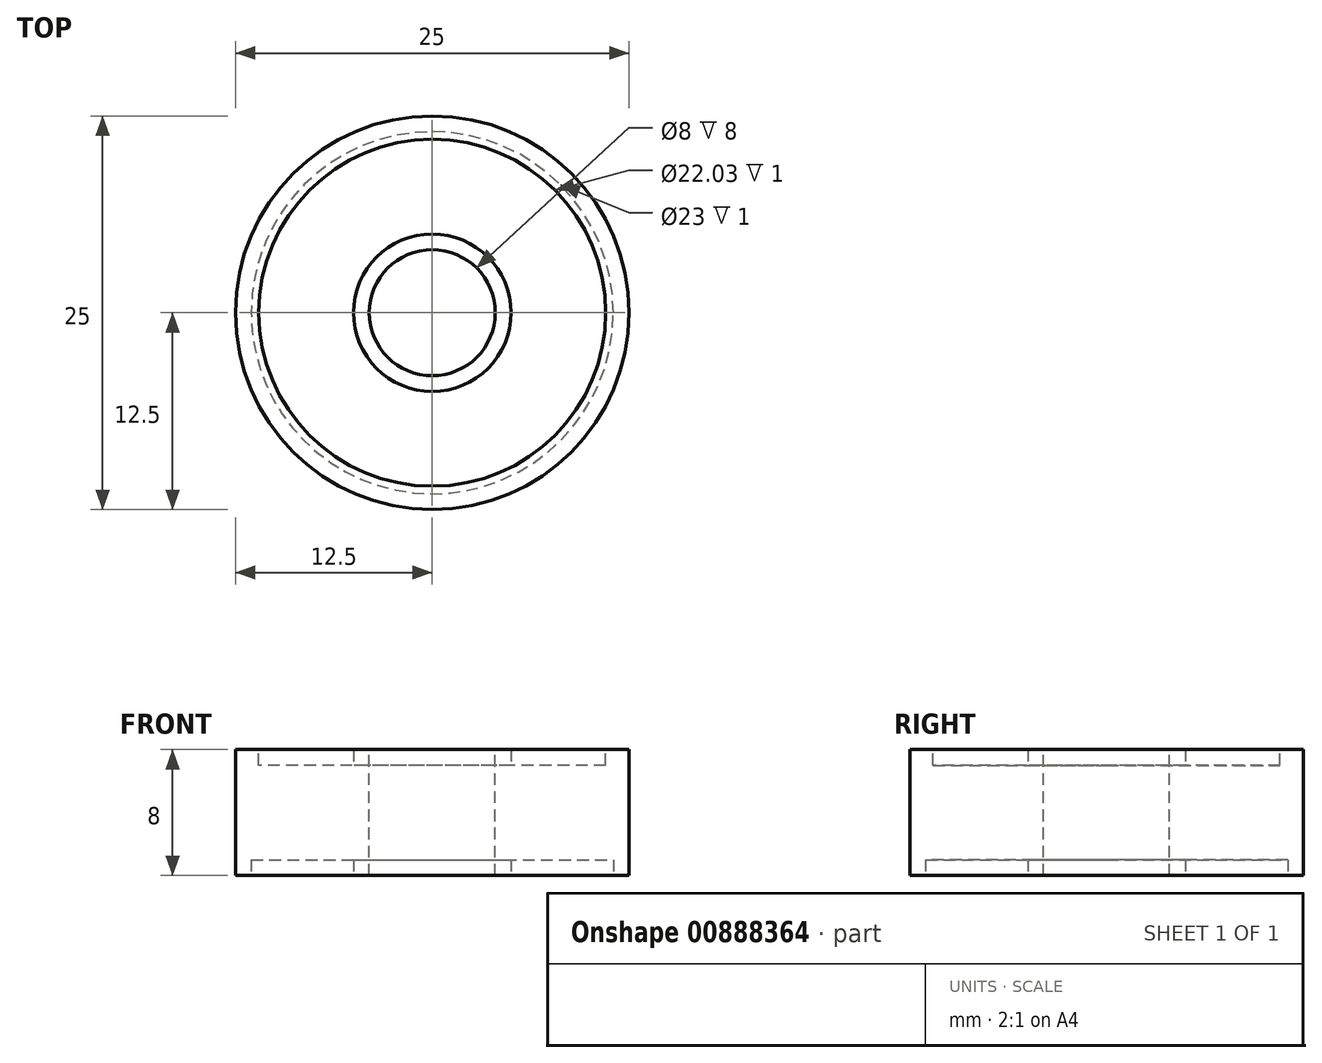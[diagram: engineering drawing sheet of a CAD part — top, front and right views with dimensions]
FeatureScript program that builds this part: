
annotation { "Feature Type Name" : "Feature", "Feature Type Description" : "" }
export const myFeature = defineFeature(function(context is Context, id is Id, definition is map)
    precondition{}
    {
        {
            var Q0;
            Q0=qCreatedBy(makeId("Top.planeOp"),FACE);
            var sketch = newSketch(context, id + "F0", { "sketchPlane" : qUnion([Q0])});
            skCircle(sketch, "E0", {"center": v(0, 0) * mm, "radius": 12.5 * mm});
            skCircle(sketch, "E1", {"center": v(0, 0) * mm, "radius": 11.5 * mm});
            skSolve(sketch);
        }
        {
            var Q0;
            Q0 = qSketchRegion(id + "F0", true);
            var Q1;
            Q1=makeQuery(id+"F0.imprint","IMPRINT",FACE,{"disambiguationData":[TD([[makeQuery(id+"F0.imprint","IMPRINT",EDGE,{"derivedFrom":sQuery(id+"F0.wireOp",EDGE,"E1")}),1.0]])]});
            extrude(context, id + "F1", {"entities" : qUnion([Q0, Q1]), "depth" : 8 * mm, "offsetDistance" : 25.4 * mm});
        }
        {
            var Q0;
            Q0=makeQuery(id+"F1.opExtrude","CAP_FACE",FACE,{"disambiguationData":[OSD([sQuery(id+"F0.wireOp",EDGE,"E0")])],"isStart":false});
            var sketch = newSketch(context, id + "F2", { "sketchPlane" : qUnion([Q0])});
            skCircle(sketch, "E2", {"center": v(0, 0) * mm, "radius": 11.02 * mm});
            skSolve(sketch);
        }
        {
            var Q0;
            Q0=makeQuery(id+"F2.imprint","IMPRINT",FACE,{"disambiguationData":[TD([[makeQuery(id+"F2.imprint","IMPRINT",EDGE,{"derivedFrom":sQuery(id+"F2.wireOp",EDGE,"E2")}),1.0]])]});
            var sketch = newSketch(context, id + "F3", { "sketchPlane" : qUnion([Q0])});
            skCircle(sketch, "E3", {"center": v(0, 0) * mm, "radius": 4 * mm});
            skCircle(sketch, "E4", {"center": v(0, 0) * mm, "radius": 5 * mm});
            skSolve(sketch);
        }
        {
            var Q0;
            Q0=makeQuery(id+"F3.imprint","IMPRINT",FACE,{"disambiguationData":[TD([[makeQuery(id+"F3.imprint","IMPRINT",EDGE,{"derivedFrom":sQuery(id+"F3.wireOp",EDGE,"E3")}),1.0]])]});
            extrude(context, id + "F4", {"entities" : qUnion([Q0]), "operationType" : NewBodyOperationType.REMOVE, "endBound" : BoundingType.THROUGH_ALL, "oppositeDirection" : true, "depth" : 25.4 * mm, "offsetDistance" : 25.4 * mm});
        }
        {
            var Q0;
            Q0=makeQuery(id+"F2.imprint","IMPRINT",FACE,{"disambiguationData":[TD([[makeQuery(id+"F2.imprint","IMPRINT",EDGE,{"derivedFrom":sQuery(id+"F2.wireOp",EDGE,"E2")}),1.0]])]});
            extrude(context, id + "F5", {"entities" : qUnion([Q0]), "operationType" : NewBodyOperationType.REMOVE, "oppositeDirection" : true, "depth" : 1 * mm, "offsetDistance" : 25.4 * mm});
        }
        {
            var Q0;
            Q0=makeQuery(id+"F5.boolean.opBoolean","COPY",FACE,{"derivedFrom":makeQuery(id+"F5.opExtrude","CAP_FACE",FACE,{"disambiguationData":[OSD([sQuery(id+"F2.wireOp",EDGE,"E2")])],"isStart":false})});
            var sketch = newSketch(context, id + "F6", { "sketchPlane" : qUnion([Q0])});
            skCircle(sketch, "E5", {"center": v(0, 0) * mm, "radius": 5 * mm});
            skSolve(sketch);
        }
        {
            var Q0;
            Q0=makeQuery(id+"F6.imprint","IMPRINT",FACE,{"disambiguationData":[TD([[makeQuery(id+"F6.imprint","IMPRINT",EDGE,{"derivedFrom":sQuery(id+"F6.wireOp",EDGE,"E5")}),1.0]])]});
            var Q1;
            Q1=sQuery(id+"F6.wireOp",EDGE,"E5");
            extrude(context, id + "F7", {"entities" : qUnion([Q0]), "operationType" : NewBodyOperationType.ADD, "surfaceEntities" : qUnion([Q1]), "depth" : 1 * mm, "offsetDistance" : 25.4 * mm});
        }
        {
            var Q0;
            Q0=makeQuery(id+"F1.opExtrude","CAP_FACE",FACE,{"disambiguationData":[OSD([sQuery(id+"F0.wireOp",EDGE,"E0")])],"isStart":true});
            var sketch = newSketch(context, id + "F8", { "sketchPlane" : qUnion([Q0])});
            skCircle(sketch, "E6", {"center": v(0, 0) * mm, "radius": 5 * mm});
            skSolve(sketch);
        }
        {
            var Q0;
            Q0=makeQuery(id+"F8.imprint","IMPRINT",FACE,{"disambiguationData":[TD([[makeQuery(id+"F8.imprint","IMPRINT",EDGE,{"derivedFrom":sQuery(id+"F8.wireOp",EDGE,"E6")}),-1.0]])]});
            var sketch = newSketch(context, id + "F9", { "sketchPlane" : qUnion([Q0])});
            skCircle(sketch, "E7", {"center": v(0, 0) * mm, "radius": 127 * mm});
            skCircle(sketch, "E8", {"center": v(0, 0) * mm, "radius": 270.84 * mm});
            skSolve(sketch);
        }
        {
            var Q0;
            Q0=makeQuery(id+"F9.imprint","IMPRINT",FACE,{"disambiguationData":[TD([[makeQuery(id+"F9.imprint","IMPRINT",EDGE,{"derivedFrom":sQuery(id+"F9.wireOp",EDGE,"E7")}),-1.0]])]});
            extrude(context, id + "F10", {"entities" : qUnion([Q0]), "operationType" : NewBodyOperationType.REMOVE, "oppositeDirection" : true, "depth" : 1 * mm, "offsetDistance" : 25.4 * mm});
        }
        {
            var Q0;
            Q0=makeQuery(id+"F8.imprint","IMPRINT",FACE,{"disambiguationData":[TD([[makeQuery(id+"F8.imprint","IMPRINT",EDGE,{"derivedFrom":sQuery(id+"F8.wireOp",EDGE,"E6")}),-1.0]])]});
            var sketch = newSketch(context, id + "F11", { "sketchPlane" : qUnion([Q0])});
            skCircle(sketch, "E9", {"center": v(0, 0) * mm, "radius": 11.5 * mm});
            skCircle(sketch, "E10", {"center": v(0, 0) * mm, "radius": 5 * mm});
            skSolve(sketch);
        }
        {
            var Q0;
            Q0 = qSketchRegion(id + "F11", true);
            extrude(context, id + "F12", {"entities" : qUnion([Q0]), "operationType" : NewBodyOperationType.REMOVE, "oppositeDirection" : true, "depth" : 1 * mm, "offsetDistance" : 25.4 * mm});
        }
    });
